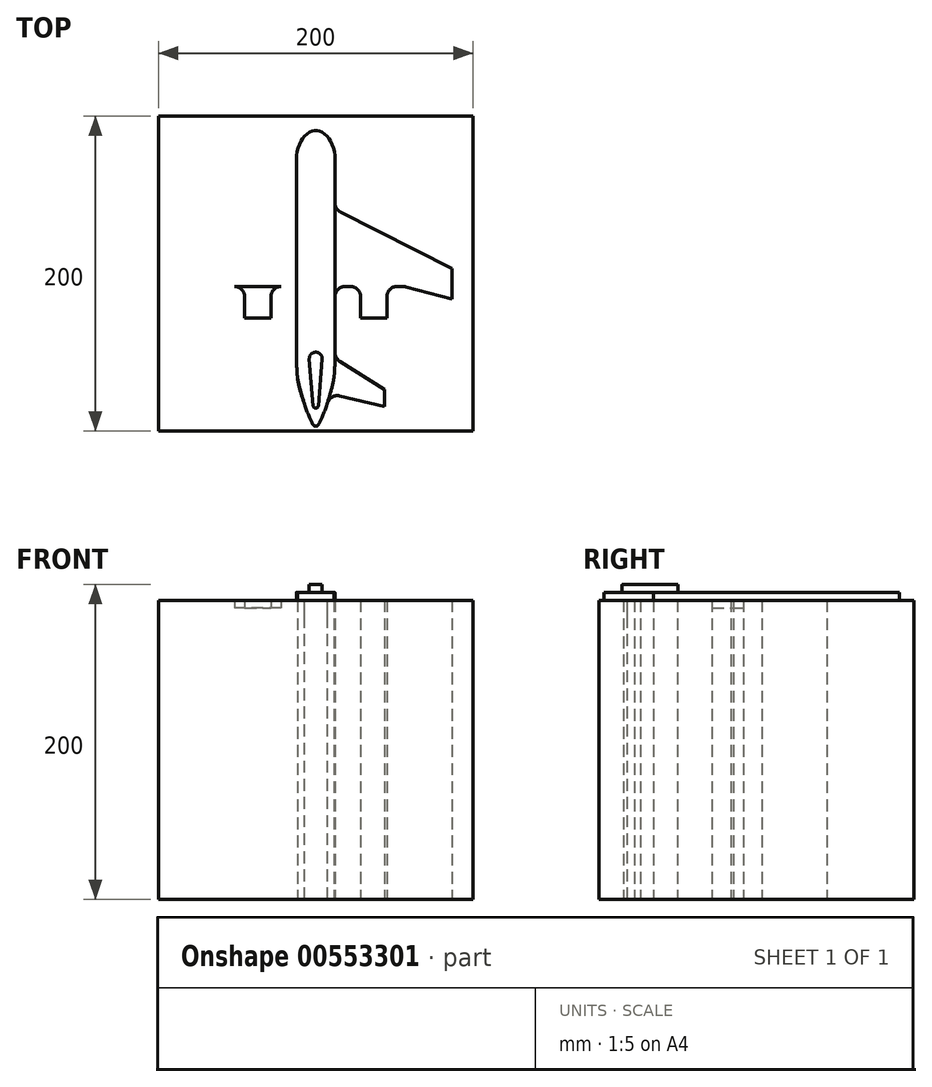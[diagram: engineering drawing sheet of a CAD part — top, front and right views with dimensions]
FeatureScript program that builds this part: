
annotation { "Feature Type Name" : "Feature", "Feature Type Description" : "" }
export const myFeature = defineFeature(function(context is Context, id is Id, definition is map)
    precondition{}
    {
        {
            var Q0;
            Q0=qCreatedBy(makeId("Top.planeOp"),FACE);
            var sketch = newSketch(context, id + "F0", { "sketchPlane" : qUnion([Q0])});
            skLineSegment(sketch, "E0.bottom", {"start": v(100, 96.72) * mm, "end": v(-100, 96.72) * mm});
            skLineSegment(sketch, "E0.top", {"start": v(100, -103.28) * mm, "end": v(-100, -103.28) * mm});
            skLineSegment(sketch, "E0.right", {"start": v(-100, 96.72) * mm, "end": v(-100, -103.28) * mm});
            skLineSegment(sketch, "E1.right", {"start": v(-12.23, 69.06) * mm, "end": v(-12.23, 41.51) * mm});
            skPoint(sketch, "E1.middle", {"position": v(0, 3.16) * mm});
            skEllipticalArc(sketch, "E2", {});
            skFitSpline(sketch, "E3", {"points": [v(-12.23, -62.74) * mm, v(-0.74, -100.07) * mm], "startDerivative": vector(0, -33.38) * mm, "endDerivative": vector(6.96, 0) * mm});
            skLineSegment(sketch, "E4", {"start": v(-15.83, 35.66) * mm, "end": v(-86.47, 0) * mm});
            skLineSegment(sketch, "E5", {"start": v(-86.47, -19.6) * mm, "end": v(-57.25, -11.7) * mm});
            skLineSegment(sketch, "E6", {"start": v(-55.6, -11.49) * mm, "end": v(-51.71, -11.49) * mm});
            skLineSegment(sketch, "E7", {"start": v(-15.28, -59.02) * mm, "end": v(-43.58, -76.9) * mm});
            skLineSegment(sketch, "E8", {"start": v(-43.58, -76.9) * mm, "end": v(-43.58, -87.8) * mm});
            skLineSegment(sketch, "E9", {"start": v(-43.58, -87.8) * mm, "end": v(-15.22, -80.95) * mm});
            skPoint(sketch, "E10.visualSharp", {"position": v(-56.44, -11.49) * mm});
            skArc(sketch, "E10.filletArc", {"start": v(-55.6, -11.49) * mm, "mid": v(-56.43, -11.54) * mm, "end": v(-57.25, -11.7) * mm});
            skLineSegment(sketch, "E11.trimOffspring", {"start": v(-12.23, -18.04) * mm, "end": v(-12.23, -53.48) * mm});
            skPoint(sketch, "E12.orphan", {"position": v(0, 43.65) * mm});
            skPoint(sketch, "E13.visualSharp", {"position": v(-12.23, -11.49) * mm});
            skArc(sketch, "E13.filletArc", {"start": v(-12.23, -18.04) * mm, "mid": v(-14.15, -13.4) * mm, "end": v(-18.78, -11.49) * mm});
            skPoint(sketch, "E14.visualSharp", {"position": v(-12.23, 37.48) * mm});
            skArc(sketch, "E14.filletArc", {"start": v(-15.83, 35.66) * mm, "mid": v(-13.2, 38.08) * mm, "end": v(-12.23, 41.51) * mm});
            skPoint(sketch, "E15.orphan", {"position": v(0, -49.37) * mm});
            skPoint(sketch, "E16.orphan", {"position": v(0, -77.28) * mm});
            skPoint(sketch, "E17.visualSharp", {"position": v(-12.23, -57.1) * mm});
            skArc(sketch, "E17.filletArc", {"start": v(-15.28, -59.02) * mm, "mid": v(-13.04, -56.65) * mm, "end": v(-12.23, -53.48) * mm});
            skPoint(sketch, "E18.visualSharp", {"position": v(-9.4, -79.55) * mm});
            skArc(sketch, "E18.filletArc", {"start": v(-7.47, -85.23) * mm, "mid": v(-10.51, -81.59) * mm, "end": v(-15.22, -80.95) * mm});
            skLineSegment(sketch, "E19.top", {"start": v(-28.5, -31.6) * mm, "end": v(-45.16, -31.6) * mm});
            skLineSegment(sketch, "E19.left", {"start": v(-28.5, -18.04) * mm, "end": v(-28.5, -31.6) * mm});
            skLineSegment(sketch, "E19.right", {"start": v(-45.16, -18.04) * mm, "end": v(-45.16, -31.6) * mm});
            skPoint(sketch, "E19.middle", {"position": v(-36.83, -11.49) * mm});
            skLineSegment(sketch, "E20.trimOffspring", {"start": v(-21.95, -11.49) * mm, "end": v(-18.78, -11.49) * mm});
            skPoint(sketch, "E21.orphan", {"position": v(-28.5, 8.63) * mm});
            skPoint(sketch, "E22.orphan", {"position": v(-45.16, 8.63) * mm});
            skPoint(sketch, "E23.visualSharp", {"position": v(-28.5, -11.49) * mm});
            skArc(sketch, "E23.filletArc", {"start": v(-21.95, -11.49) * mm, "mid": v(-26.58, -13.4) * mm, "end": v(-28.5, -18.04) * mm});
            skPoint(sketch, "E24.visualSharp", {"position": v(-45.16, -11.49) * mm});
            skArc(sketch, "E24.filletArc", {"start": v(-45.16, -18.04) * mm, "mid": v(-47.08, -13.4) * mm, "end": v(-51.71, -11.49) * mm});
            skPoint(sketch, "E1.left.end.orphan", {"position": v(12.23, -62.74) * mm});
            skLineSegment(sketch, "E25.MirrorCS", {"start": v(12.23, 69.06) * mm, "end": v(12.23, 41.51) * mm});
            skArc(sketch, "E26.MirrorCS", {"start": v(15.83, 35.66) * mm, "mid": v(13.2, 38.08) * mm, "end": v(12.23, 41.51) * mm});
            skLineSegment(sketch, "E27.MirrorCS", {"start": v(15.83, 35.66) * mm, "end": v(86.47, 0) * mm});
            skLineSegment(sketch, "E28.MirrorCS", {"start": v(86.47, -19.6) * mm, "end": v(57.25, -11.7) * mm});
            skArc(sketch, "E29.MirrorCS", {"start": v(55.6, -11.49) * mm, "mid": v(56.43, -11.54) * mm, "end": v(57.25, -11.7) * mm});
            skLineSegment(sketch, "E30.MirrorCS", {"start": v(55.6, -11.49) * mm, "end": v(51.71, -11.49) * mm});
            skArc(sketch, "E31.MirrorCS", {"start": v(45.16, -18.04) * mm, "mid": v(47.08, -13.4) * mm, "end": v(51.71, -11.49) * mm});
            skArc(sketch, "E32.MirrorCS", {"start": v(21.95, -11.49) * mm, "mid": v(26.58, -13.4) * mm, "end": v(28.5, -18.04) * mm});
            skLineSegment(sketch, "E33.MirrorCS", {"start": v(21.95, -11.49) * mm, "end": v(18.78, -11.49) * mm});
            skArc(sketch, "E34.MirrorCS", {"start": v(12.23, -18.04) * mm, "mid": v(14.15, -13.4) * mm, "end": v(18.78, -11.49) * mm});
            skLineSegment(sketch, "E35.MirrorCS", {"start": v(12.23, -18.04) * mm, "end": v(12.23, -53.48) * mm});
            skLineSegment(sketch, "E36.MirrorCS", {"start": v(28.5, -18.04) * mm, "end": v(28.5, -31.6) * mm});
            skLineSegment(sketch, "E37.MirrorCS", {"start": v(28.5, -31.6) * mm, "end": v(45.16, -31.6) * mm});
            skLineSegment(sketch, "E38.MirrorCS", {"start": v(45.16, -18.04) * mm, "end": v(45.16, -31.6) * mm});
            skArc(sketch, "E39.MirrorCS", {"start": v(15.28, -59.02) * mm, "mid": v(13.04, -56.65) * mm, "end": v(12.23, -53.48) * mm});
            skLineSegment(sketch, "E40.MirrorCS", {"start": v(15.28, -59.02) * mm, "end": v(43.58, -76.9) * mm});
            skLineSegment(sketch, "E41.MirrorCS", {"start": v(43.58, -76.9) * mm, "end": v(43.58, -87.8) * mm});
            skLineSegment(sketch, "E42.MirrorCS", {"start": v(43.58, -87.8) * mm, "end": v(15.22, -80.95) * mm});
            skArc(sketch, "E43.MirrorCS", {"start": v(7.47, -85.23) * mm, "mid": v(10.51, -81.59) * mm, "end": v(15.22, -80.95) * mm});
            skFitSpline(sketch, "E44.MirrorCS", {"points": [v(12.19, -63.2) * mm, v(0.74, -100.07) * mm], "startDerivative": vector(-0.07, -32.57) * mm, "endDerivative": vector(-6.87, 0) * mm});
            skLineSegment(sketch, "E45", {"start": v(-12.23, 41.51) * mm, "end": v(-12.23, -18.04) * mm});
            skLineSegment(sketch, "E46", {"start": v(12.23, 41.51) * mm, "end": v(12.23, -18.04) * mm});
            skLineSegment(sketch, "E47", {"start": v(-51.71, -11.49) * mm, "end": v(-21.95, -11.49) * mm});
            skLineSegment(sketch, "E48", {"start": v(21.95, -11.49) * mm, "end": v(51.71, -11.49) * mm});
            skFitSpline(sketch, "E49", {"points": [v(-12.23, -53.48) * mm, v(-7.47, -85.23) * mm], "startDerivative": vector(0, -61.15) * mm, "endDerivative": vector(8.6, -25.51) * mm});
            skFitSpline(sketch, "E50.MirrorCS", {"points": [v(12.23, -53.48) * mm, v(7.47, -85.23) * mm], "startDerivative": vector(0, -61.15) * mm, "endDerivative": vector(-8.6, -25.51) * mm});
            skLineSegment(sketch, "E51", {"start": v(-86.47, 0) * mm, "end": v(-86.47, -19.6) * mm});
            skPoint(sketch, "E52.start.orphan", {"position": v(-100, -6.83) * mm});
            skPoint(sketch, "E53.orphan", {"position": v(-100, -23.25) * mm});
            skLineSegment(sketch, "E54.MirrorCS", {"start": v(86.47, 0) * mm, "end": v(86.47, -19.6) * mm});
            skLineSegment(sketch, "E55", {"start": v(100, 96.72) * mm, "end": v(100, -103.28) * mm});
            skLineSegment(sketch, "E56", {"start": v(-0.74, -100.07) * mm, "end": v(0.74, -100.07) * mm});
            const initialGuessF0  = {"E2": [0, 0.06906486302614212, 0, 1, 0.018457970943929935, 0.012229328043758878, 4.71238898038469, 1.5707963267948966]};
            skSetInitialGuess(sketch, initialGuessF0);
            skSolve(sketch);
        }
        {
            var Q0;
            Q0=makeQuery(id+"F0.imprint","IMPRINT",FACE,{"disambiguationData":[TD([[makeQuery(id+"F0.imprint","IMPRINT",EDGE,{"derivedFrom":sQuery(id+"F0.wireOp",EDGE,"E4")}),1.0]])]});
            var Q1;
            Q1=makeQuery(id+"F0.imprint","IMPRINT",FACE,{"disambiguationData":[TD([[makeQuery(id+"F0.imprint","IMPRINT",EDGE,{"derivedFrom":sQuery(id+"F0.wireOp",EDGE,"E1.right")}),1.0]])]});
            var Q2;
            Q2=makeQuery(id+"F0.imprint","IMPRINT",FACE,{"disambiguationData":[TD([[makeQuery(id+"F0.imprint","IMPRINT",EDGE,{"derivedFrom":sQuery(id+"F0.wireOp",EDGE,"E26.MirrorCS")}),1.0]])]});
            var Q3;
            Q3=makeQuery(id+"F0.imprint","IMPRINT",FACE,{"disambiguationData":[TD([[makeQuery(id+"F0.imprint","IMPRINT",EDGE,{"derivedFrom":sQuery(id+"F0.wireOp",EDGE,"E31.MirrorCS")}),1.0]])]});
            var Q4;
            Q4=makeQuery(id+"F0.imprint","IMPRINT",FACE,{"disambiguationData":[TD([[makeQuery(id+"F0.imprint","IMPRINT",EDGE,{"derivedFrom":sQuery(id+"F0.wireOp",EDGE,"E19.top")}),-1.0]])]});
            var Q5;
            Q5=makeQuery(id+"F0.imprint","IMPRINT",FACE,{"disambiguationData":[TD([[makeQuery(id+"F0.imprint","IMPRINT",EDGE,{"derivedFrom":sQuery(id+"F0.wireOp",EDGE,"E7")}),1.0]])]});
            var Q6;
            Q6=makeQuery(id+"F0.imprint","IMPRINT",FACE,{"disambiguationData":[TD([[makeQuery(id+"F0.imprint","IMPRINT",EDGE,{"derivedFrom":sQuery(id+"F0.wireOp",EDGE,"E39.MirrorCS")}),1.0]])]});
            var Q7;
            Q7=makeQuery(id+"F0.imprint","IMPRINT",FACE,{"disambiguationData":[TD([[makeQuery(id+"F0.imprint","IMPRINT",EDGE,{"derivedFrom":sQuery(id+"F0.wireOp",EDGE,"E0.bottom")}),1.0]])]});
            extrude(context, id + "F1", {"entities" : qUnion([Q0, Q1, Q2, Q3, Q4, Q5, Q6, Q7]), "depth" : 180 * mm, "offsetDistance" : 25 * mm});
        }
        {
            var Q0;
            Q0=makeQuery(id+"F0.imprint","IMPRINT",FACE,{"disambiguationData":[TD([[makeQuery(id+"F0.imprint","IMPRINT",EDGE,{"derivedFrom":sQuery(id+"F0.wireOp",EDGE,"E4")}),1.0]])]});
            var Q1;
            Q1=makeQuery(id+"F0.imprint","IMPRINT",FACE,{"disambiguationData":[TD([[makeQuery(id+"F0.imprint","IMPRINT",EDGE,{"derivedFrom":sQuery(id+"F0.wireOp",EDGE,"E19.top")}),-1.0]])]});
            var Q2;
            Q2=makeQuery(id+"F0.imprint","IMPRINT",FACE,{"disambiguationData":[TD([[makeQuery(id+"F0.imprint","IMPRINT",EDGE,{"derivedFrom":sQuery(id+"F0.wireOp",EDGE,"E1.right")}),1.0]])]});
            var Q3;
            Q3=makeQuery(id+"F0.imprint","IMPRINT",FACE,{"disambiguationData":[TD([[makeQuery(id+"F0.imprint","IMPRINT",EDGE,{"derivedFrom":sQuery(id+"F0.wireOp",EDGE,"E26.MirrorCS")}),1.0]])]});
            var Q4;
            Q4=makeQuery(id+"F0.imprint","IMPRINT",FACE,{"disambiguationData":[TD([[makeQuery(id+"F0.imprint","IMPRINT",EDGE,{"derivedFrom":sQuery(id+"F0.wireOp",EDGE,"E31.MirrorCS")}),1.0]])]});
            var Q5;
            Q5=makeQuery(id+"F0.imprint","IMPRINT",FACE,{"disambiguationData":[TD([[makeQuery(id+"F0.imprint","IMPRINT",EDGE,{"derivedFrom":sQuery(id+"F0.wireOp",EDGE,"E39.MirrorCS")}),1.0]])]});
            var Q6;
            Q6=makeQuery(id+"F0.imprint","IMPRINT",FACE,{"disambiguationData":[TD([[makeQuery(id+"F0.imprint","IMPRINT",EDGE,{"derivedFrom":sQuery(id+"F0.wireOp",EDGE,"E7")}),1.0]])]});
            extrude(context, id + "F2", {"entities" : qUnion([Q0, Q1, Q2, Q3, Q4, Q5, Q6]), "operationType" : NewBodyOperationType.ADD, "depth" : 185 * mm, "offsetDistance" : 25 * mm});
        }
        {
            var Q0;
            Q0=makeQuery(id+"F0.imprint","IMPRINT",FACE,{"disambiguationData":[TD([[makeQuery(id+"F0.imprint","IMPRINT",EDGE,{"derivedFrom":sQuery(id+"F0.wireOp",EDGE,"E1.right")}),1.0]])]});
            var Q1;
            Q1=makeQuery(id+"F0.imprint","IMPRINT",FACE,{"disambiguationData":[TD([[makeQuery(id+"F0.imprint","IMPRINT",EDGE,{"derivedFrom":sQuery(id+"F0.wireOp",EDGE,"E4")}),1.0]])]});
            var Q2;
            Q2=makeQuery(id+"F0.imprint","IMPRINT",FACE,{"disambiguationData":[TD([[makeQuery(id+"F0.imprint","IMPRINT",EDGE,{"derivedFrom":sQuery(id+"F0.wireOp",EDGE,"E26.MirrorCS")}),1.0]])]});
            var Q3;
            Q3=makeQuery(id+"F0.imprint","IMPRINT",FACE,{"disambiguationData":[TD([[makeQuery(id+"F0.imprint","IMPRINT",EDGE,{"derivedFrom":sQuery(id+"F0.wireOp",EDGE,"E39.MirrorCS")}),1.0]])]});
            var Q4;
            Q4=makeQuery(id+"F0.imprint","IMPRINT",FACE,{"disambiguationData":[TD([[makeQuery(id+"F0.imprint","IMPRINT",EDGE,{"derivedFrom":sQuery(id+"F0.wireOp",EDGE,"E7")}),1.0]])]});
            extrude(context, id + "F3", {"entities" : qUnion([Q0, Q1, Q2, Q3, Q4]), "operationType" : NewBodyOperationType.ADD, "depth" : 190 * mm, "offsetDistance" : 25 * mm});
        }
        {
            var Q0;
            Q0=makeQuery(id+"F0.imprint","IMPRINT",FACE,{"disambiguationData":[TD([[makeQuery(id+"F0.imprint","IMPRINT",EDGE,{"derivedFrom":sQuery(id+"F0.wireOp",EDGE,"E1.right")}),1.0]])]});
            extrude(context, id + "F4", {"entities" : qUnion([Q0]), "operationType" : NewBodyOperationType.ADD, "depth" : 195 * mm, "offsetDistance" : 25 * mm});
        }
        {
            var Q0;
            Q0=makeQuery(id+"F4.opExtrude","CAP_FACE",FACE,{"disambiguationData":[OSD([sQuery(id+"F0.wireOp",EDGE,"E1.right"),sQuery(id+"F0.wireOp",EDGE,"E2"),sQuery(id+"F0.wireOp",EDGE,"E3"),sQuery(id+"F0.wireOp",EDGE,"E11.trimOffspring"),sQuery(id+"F0.wireOp",EDGE,"E25.MirrorCS"),sQuery(id+"F0.wireOp",EDGE,"E35.MirrorCS"),sQuery(id+"F0.wireOp",EDGE,"E44.MirrorCS"),sQuery(id+"F0.wireOp",EDGE,"E45"),sQuery(id+"F0.wireOp",EDGE,"E46"),sQuery(id+"F0.wireOp",EDGE,"E49"),sQuery(id+"F0.wireOp",EDGE,"E50.MirrorCS"),sQuery(id+"F0.wireOp",EDGE,"E56")])],"isStart":false});
            var sketch = newSketch(context, id + "F5", { "sketchPlane" : qUnion([Q0])});
            skLineSegment(sketch, "E57", {"start": v(-4.12, -57.7) * mm, "end": v(-1.63, -87.27) * mm});
            skLineSegment(sketch, "E58.MirrorCS", {"start": v(4.12, -57.7) * mm, "end": v(1.63, -87.27) * mm});
            skArc(sketch, "E59", {"start": v(-1.63, -87.27) * mm, "mid": v(0, -88.77) * mm, "end": v(1.63, -87.27) * mm});
            skArc(sketch, "E60", {"start": v(4.12, -57.7) * mm, "mid": v(0, -53.21) * mm, "end": v(-4.12, -57.7) * mm});
            skSolve(sketch);
        }
        {
            var Q0;
            Q0=makeQuery(id+"F5.imprint","IMPRINT",FACE,{"disambiguationData":[TD([[makeQuery(id+"F5.imprint","IMPRINT",EDGE,{"derivedFrom":sQuery(id+"F5.wireOp",EDGE,"E57")}),1.0]])]});
            extrude(context, id + "F6", {"entities" : qUnion([Q0]), "operationType" : NewBodyOperationType.ADD, "depth" : 5 * mm, "offsetDistance" : 25 * mm});
        }
    });
